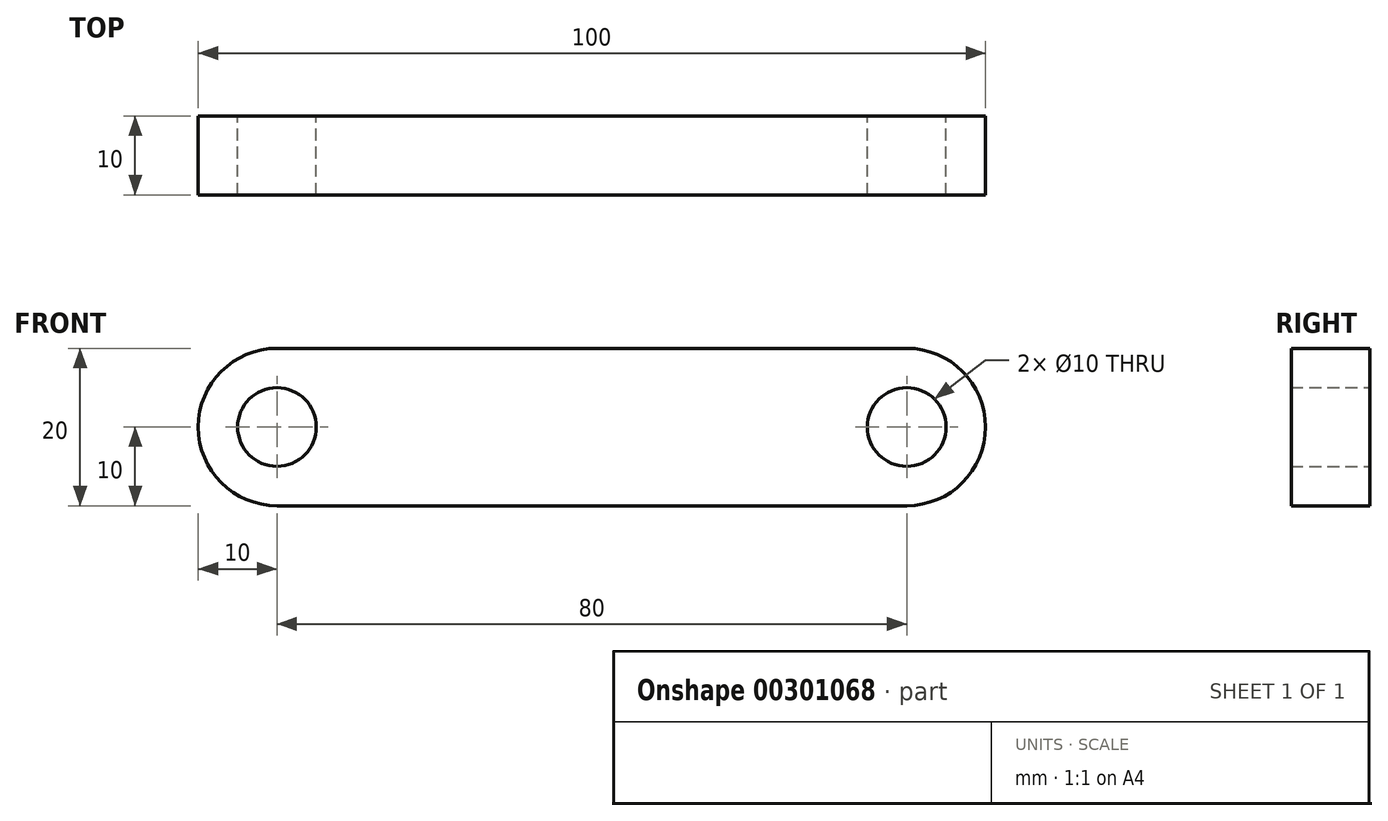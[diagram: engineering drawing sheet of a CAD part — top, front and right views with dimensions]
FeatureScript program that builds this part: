
annotation { "Feature Type Name" : "Feature", "Feature Type Description" : "" }
export const myFeature = defineFeature(function(context is Context, id is Id, definition is map)
    precondition{}
    {
        {
            var Q0;
            Q0=qCreatedBy(makeId("Front.planeOp"),FACE);
            var sketch = newSketch(context, id + "F0", { "sketchPlane" : qUnion([Q0])});
            skArc(sketch, "E0", {"start": v(0, 20) * mm, "mid": v(-10, 10) * mm, "end": v(0, 0) * mm});
            skLineSegment(sketch, "E1", {"start": v(0, 20) * mm, "end": v(80, 20) * mm});
            skLineSegment(sketch, "E2", {"start": v(0, 0) * mm, "end": v(80, 0) * mm});
            skArc(sketch, "E3", {"start": v(80, 0) * mm, "mid": v(90, 10) * mm, "end": v(80, 20) * mm});
            skCircle(sketch, "E4", {"center": v(0, 10) * mm, "radius": 5 * mm});
            skCircle(sketch, "E5", {"center": v(80, 10) * mm, "radius": 5 * mm});
            skSolve(sketch);
        }
        {
            var Q0;
            Q0 = qSketchRegion(id + "F0", true);
            extrude(context, id + "F1", {"entities" : qUnion([Q0]), "depth" : 10 * mm});
        }
    });
